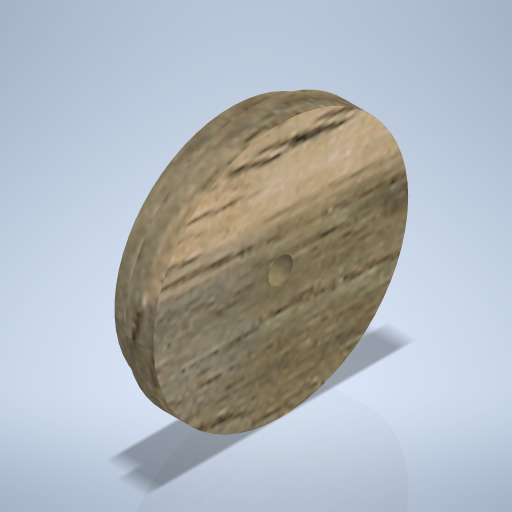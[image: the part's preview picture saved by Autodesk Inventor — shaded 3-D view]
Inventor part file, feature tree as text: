
AUTODESK INVENTOR PART (.ipt)
format: ipt  version: 2024 (Build 280153000, 153)  size: 413,696 bytes
history: native  units: mm
features: sketch x2, revolve x1, extrude x1
ambient origin geometry x8: Origin, YZ Plane, XZ Plane, XY Plane, X Axis, Y Axis, Z Axis, Center Point
bodies: Volumenkörper1 (feature_tree)
feature tree (4):
  revolve  "Umdrehung1"
  extrude  "Extrusion1"  Depth=4.0mm
  sketch  "Skizze1"  dims[d0=3.0mm d1=4.0mm]
  sketch  "Skizze2"  dims[d2=36.0mm d3=33.0mm d4=90.0deg d5=3.5mm d6=10.0mm d7=0.0mm]
